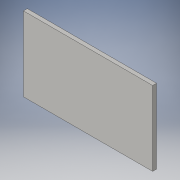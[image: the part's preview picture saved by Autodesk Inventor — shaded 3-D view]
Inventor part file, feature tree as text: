
AUTODESK INVENTOR PART (.ipt)
format: ipt  version: 2016 (Build 200138000, 138)  size: 89,088 bytes
history: native  units: in
note: dims shown in document units (in); Inventor stores cm internally (conversion verified against a paired STEP export)
features: extrude x1, sketch x1
ambient origin geometry x8: Origin, YZ Plane, XZ Plane, XY Plane, X Axis, Y Axis, Z Axis, Center Point
bodies: Solid1 (feature_tree)
feature tree (2):
  extrude  "Extrusion1"  Depth=0.5in TaperAngle=0.0deg
  sketch  "Sketch1"  dims[d0=16.5in d2=0.5in d3=0.0in]
